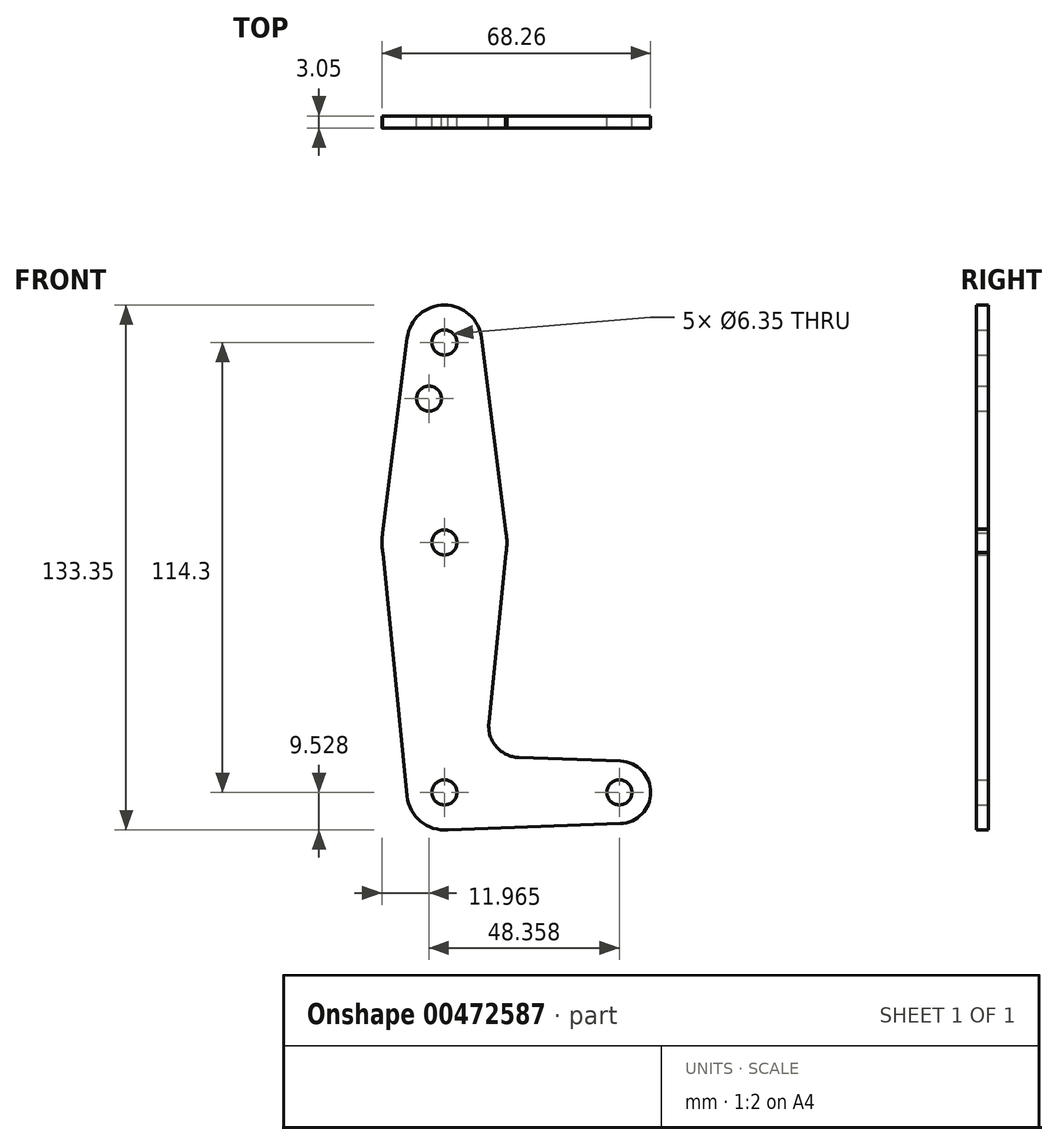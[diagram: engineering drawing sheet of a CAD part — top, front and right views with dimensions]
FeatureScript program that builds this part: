
annotation { "Feature Type Name" : "Feature", "Feature Type Description" : "" }
export const myFeature = defineFeature(function(context is Context, id is Id, definition is map)
    precondition{}
    {
        {
            var Q0;
            Q0=qCreatedBy(makeId("Front.planeOp"),FACE);
            var sketch = newSketch(context, id + "F0", { "sketchPlane" : qUnion([Q0])});
            skLineSegment(sketch, "E0", {"start": v(-21.7, 60.33) * mm, "end": v(-21.7, -53.97) * mm, "construction": true});
            skLineSegment(sketch, "E1", {"start": v(-21.7, -53.97) * mm, "end": v(22.74, -53.97) * mm, "construction": true});
            skCircle(sketch, "E2", {"center": v(-21.7, 60.33) * mm, "radius": 9.53 * mm});
            skCircle(sketch, "E3", {"center": v(-21.7, 9.53) * mm, "radius": 15.88 * mm});
            skCircle(sketch, "E4", {"center": v(-21.7, -53.97) * mm, "radius": 9.53 * mm});
            skCircle(sketch, "E5", {"center": v(22.74, -53.97) * mm, "radius": 7.94 * mm});
            skLineSegment(sketch, "E6", {"start": v(-5.84, 8.94) * mm, "end": v(-10.4, -36.38) * mm});
            skLineSegment(sketch, "E7", {"start": v(-21.96, -63.5) * mm, "end": v(23.02, -61.9) * mm});
            skLineSegment(sketch, "E8", {"start": v(-6.2, 12.92) * mm, "end": v(-12.26, 61.5) * mm});
            skLineSegment(sketch, "E9", {"start": v(-37.4, 11.96) * mm, "end": v(-31.16, 61.52) * mm});
            skLineSegment(sketch, "E10", {"start": v(-37.35, 6.83) * mm, "end": v(-31.19, -54.92) * mm});
            skLineSegment(sketch, "E11", {"start": v(-2.78, -45.12) * mm, "end": v(23.03, -46.04) * mm});
            skCircle(sketch, "E12", {"center": v(-21.7, 60.33) * mm, "radius": 3.18 * mm});
            skCircle(sketch, "E13", {"center": v(-21.7, 9.53) * mm, "radius": 3.18 * mm});
            skCircle(sketch, "E14", {"center": v(-21.7, -53.97) * mm, "radius": 3.18 * mm});
            skCircle(sketch, "E15", {"center": v(22.74, -53.97) * mm, "radius": 3.18 * mm});
            skCircle(sketch, "E16", {"center": v(-25.62, 46.05) * mm, "radius": 3.18 * mm});
            skArc(sketch, "E17.filletArc", {"start": v(-10.4, -36.38) * mm, "mid": v(-8.49, -42.4) * mm, "end": v(-2.78, -45.12) * mm});
            skSolve(sketch);
        }
        {
            var Q0;
            Q0 = qSketchRegion(id + "F0", true);
            extrude(context, id + "F1", {"entities" : qUnion([Q0]), "depth" : 3.05 * mm});
        }
    });
